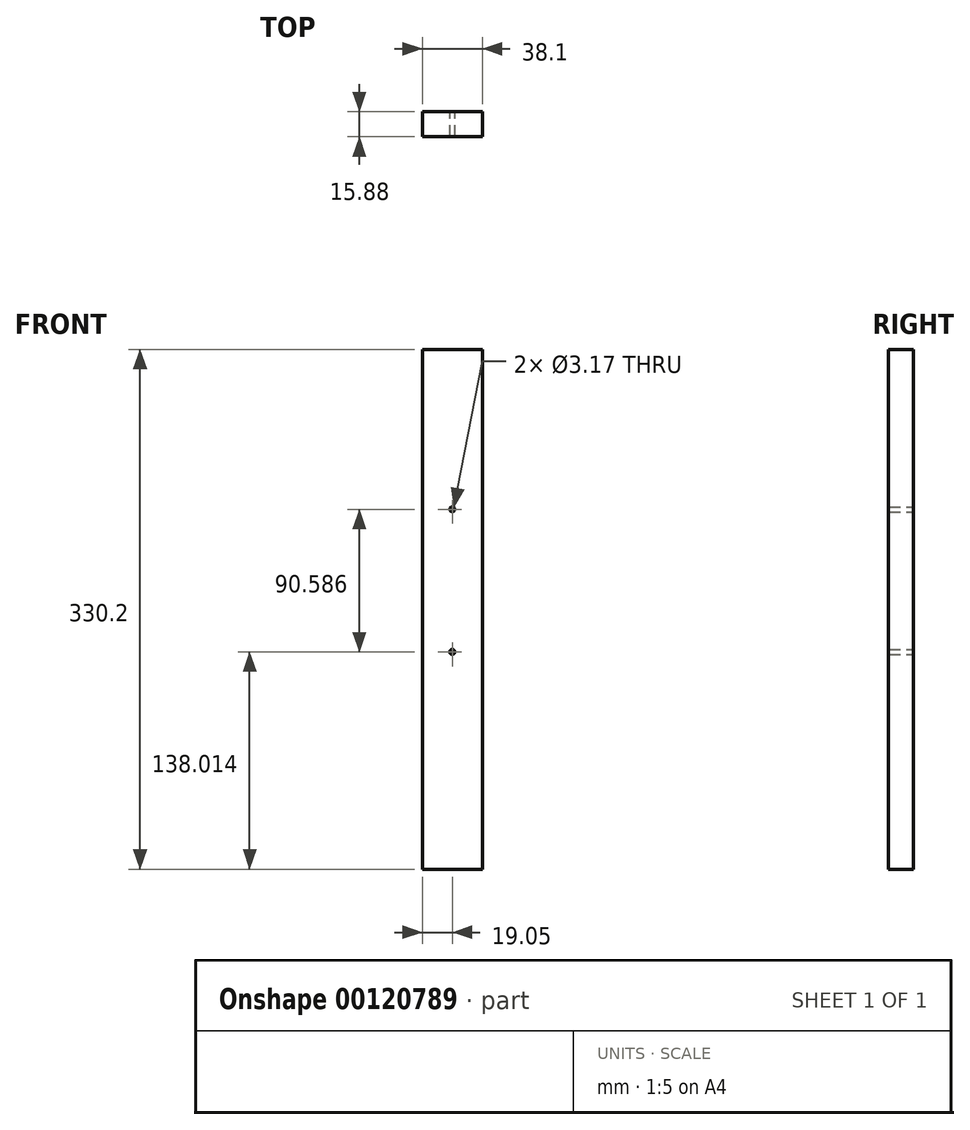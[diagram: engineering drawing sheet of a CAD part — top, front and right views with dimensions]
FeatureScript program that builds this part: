
annotation { "Feature Type Name" : "Feature", "Feature Type Description" : "" }
export const myFeature = defineFeature(function(context is Context, id is Id, definition is map)
    precondition{}
    {
        {
            var Q0;
            Q0=qCreatedBy(makeId("Front.planeOp"),FACE);
            var sketch = newSketch(context, id + "F0", { "sketchPlane" : qUnion([Q0])});
            skLineSegment(sketch, "E0.bottom", {"start": v(-19.05, 165.1) * mm, "end": v(19.05, 165.1) * mm});
            skLineSegment(sketch, "E0.top", {"start": v(-19.05, -165.1) * mm, "end": v(19.05, -165.1) * mm});
            skLineSegment(sketch, "E0.left", {"start": v(-19.05, 165.1) * mm, "end": v(-19.05, -165.1) * mm});
            skLineSegment(sketch, "E0.right", {"start": v(19.05, 165.1) * mm, "end": v(19.05, -165.1) * mm});
            skPoint(sketch, "E0.middle", {"position": v(0, 0) * mm});
            skCircle(sketch, "E1", {"center": v(0, 63.5) * mm, "radius": 1.59 * mm});
            skCircle(sketch, "E2", {"center": v(0, -27.09) * mm, "radius": 1.59 * mm});
            skSolve(sketch);
        }
        {
            var Q0;
            Q0=makeQuery(id+"F0.imprint","IMPRINT",FACE,{"disambiguationData":[TD([[makeQuery(id+"F0.imprint","IMPRINT",EDGE,{"derivedFrom":sQuery(id+"F0.wireOp",EDGE,"E0.bottom")}),-1.0]])]});
            extrude(context, id + "F1", {"entities" : qUnion([Q0]), "endBound" : BoundingType.SYMMETRIC, "depth" : 15.88 * mm});
        }
    });
